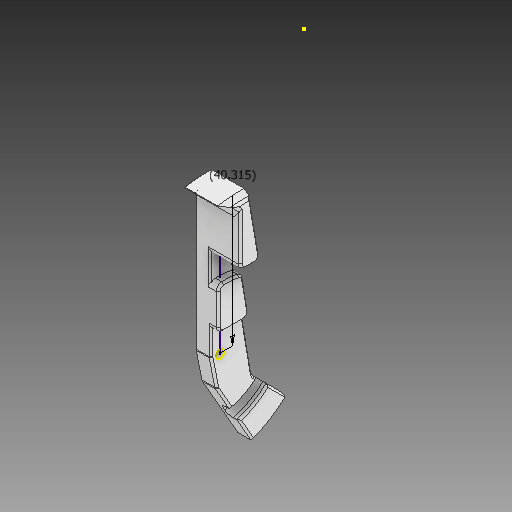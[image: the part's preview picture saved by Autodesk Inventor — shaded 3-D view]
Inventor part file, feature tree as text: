
AUTODESK INVENTOR PART (.ipt)
format: ipt  version: 2020 (Build 240168000, 168)  size: 180,224 bytes
history: native  units: in
note: dims shown in document units (in); Inventor stores cm internally (conversion verified against a paired STEP export)
features: sketch x1, imported_body x1
ambient origin geometry x8: Origin, YZ Plane, XZ Plane, XY Plane, X Axis, Y Axis, Z Axis, Center Point
bodies: Solid1 (feature_tree)
feature tree (2):
  sketch  "Sketch1"  dims[d0=1.5872in]
  imported_body  "Base1"
